# Revit family: Serene_T&T_Window_D_Standard
name_source: partatom
category: Windows
revit_build: Autodesk Revit 2014 (Build: 20130308_1515(x64)
units: mm (PartAtom-declared; Revit-internal decimal feet)

## types (6) — shared parameters
Area Glazing Sash = 0.43 m²
Custom Sash Height = 1122 mm  [stored 3.6811 ft]
Custom Window Width = 590 mm  [stored 1.9357 ft]
DG Gasket Finish = Double Glazing Gasket Material
DG Gasket Thickness = 12 mm  [stored 0.0393701 ft]
DG Thickness Calc = 4 mm  [stored 0.0131234 ft]
Default Sill Height = 800 mm  [stored 2.62467 ft]
Description = Tilt and turn window, Type D
Fixed Panel Width = 510 mm  [stored 1.67323 ft]
Frame Thickness = 52 mm
Length Transom = 510 mm  [stored 1.67323 ft]
Limit Fixed Panel Height Max = 1800 mm  [stored 5.90551 ft]
Limit Fixed Panel Height Min = 200 mm  [stored 0.656168 ft]
Limit Sash Height Max = 1500 mm  [stored 4.92126 ft]
Limit Sash Height Min = 300 mm  [stored 0.984252 ft]
Limit Sash Width Max = 700 mm  [stored 2.29659 ft]
Limit Sash Width Min = 300 mm  [stored 0.984252 ft]
Limit Window Height Max = 3030 mm
Limit Window Height Min = 1430 mm
Limit Window Width Max = 768 mm  [stored 2.51969 ft]
Limit Window Width Min = 368 mm  [stored 1.20735 ft]
Manufacturer = Crealco
Max Pane Area = 0.43 m²
Max System DG One Piece Thickness = 4 mm  [stored 0.0131234 ft]
Max System DG Unit Thickness = 20 mm  [stored 0.0656168 ft]
Model = Serene
Sash Edge Gap = 34 mm
Sash Frame Gasket = 3 mm  [stored 0.00984252 ft]
Sash Height = 1122 mm  [stored 3.6811 ft]
Sash Width = 522 mm  [stored 1.7126 ft]
URL = http://www.crealco.co.za
Wall Closure = By host
Width = 590 mm  [stored 1.9357 ft]
zero-valued in all types: Custom Window Exterior Offset

## per-type parameters (varying)
| type | Area Glazing Fixed Panel | Clearvue Insulated LowE SHGC Value | Clearvue Insulated LowE U Value | Clearvue Insulated SHGC Value | Clearvue Insulated U Value | Clearvue SHGC Value | Clearvue U Value | Custom Windload | Custom Window Height | Energy Advantage SHGC Value | Energy Advantage U Value | Fixed Panel Height | Height | Intruderprufe LowE SHGC Value | Intruderprufe LowE U Value | Intruderprufe SHGC Value | Intruderprufe U Value | Windload Design |
| 52TT-0615S-1000Pa | 0.13 m² | 0.394 | 4.24 | 0.431 | 4.63 | 0.484 | 6.4 | 1000 mm  [stored 3.28084 ft] | 1490 mm  [stored 4.88845 ft] | 0.436 | 5.57 | 260 mm | 1490 mm  [stored 4.88845 ft] | 0.398 | 4.68 | 0.449 | 6.29 | 1000 mm  [stored 3.28084 ft] |
| 52TT-0615S-1500Pa | 0.13 m² | 0.394 | 4.24 | 0.431 | 4.63 | 0.484 | 6.4 | 1500 mm  [stored 4.92126 ft] | 1490 mm  [stored 4.88845 ft] | 0.436 | 5.57 | 260 mm | 1490 mm  [stored 4.88845 ft] | 0.398 | 4.68 | 0.449 | 6.29 | 1500 mm  [stored 4.92126 ft] |
| 52TT-0615S-2000Pa | 0.13 m² | 0.394 | 4.24 | 0.431 | 4.63 | 0.484 | 6.4 | 2000 mm  [stored 6.56168 ft] | 1490 mm  [stored 4.88845 ft] | 0.436 | 5.57 | 260 mm | 1490 mm  [stored 4.88845 ft] | 0.398 | 4.68 | 0.449 | 6.29 | 2000 mm  [stored 6.56168 ft] |
| 52TT-0618S-1000Pa | 0.28 m² | 0.418 | 4.04 | 0.458 | 4.46 | 0.515 | 6.33 | 1000 mm  [stored 3.28084 ft] | 1790 mm  [stored 5.8727 ft] | 0.463 | 5.44 | 560 mm | 1790 mm  [stored 5.8727 ft] | 0.423 | 4.62 | 0.477 | 6.22 | 1000 mm  [stored 3.28084 ft] |
| 52TT-0618S-1500Pa | 0.28 m² | 0.418 | 4.04 | 0.458 | 4.46 | 0.515 | 6.33 | 1500 mm  [stored 4.92126 ft] | 1790 mm  [stored 5.8727 ft] | 0.463 | 5.44 | 560 mm | 1790 mm  [stored 5.8727 ft] | 0.423 | 4.62 | 0.477 | 6.22 | 1500 mm  [stored 4.92126 ft] |
| 52TT-0618S-2000Pa | 0.28 m² | 0.418 | 4.04 | 0.458 | 4.46 | 0.515 | 6.33 | 2000 mm  [stored 6.56168 ft] | 1790 mm  [stored 5.8727 ft] | 0.463 | 5.44 | 560 mm | 1790 mm  [stored 5.8727 ft] | 0.423 | 4.62 | 0.477 | 6.22 | 2000 mm  [stored 6.56168 ft] |

note: [stored X ft] marks values corroborated as IEEE doubles in the binary element streams (Revit-internal decimal feet)

## geometry (parser evidence)
native form markers: Sweep x30
no freeform markers — native parametric forms only
